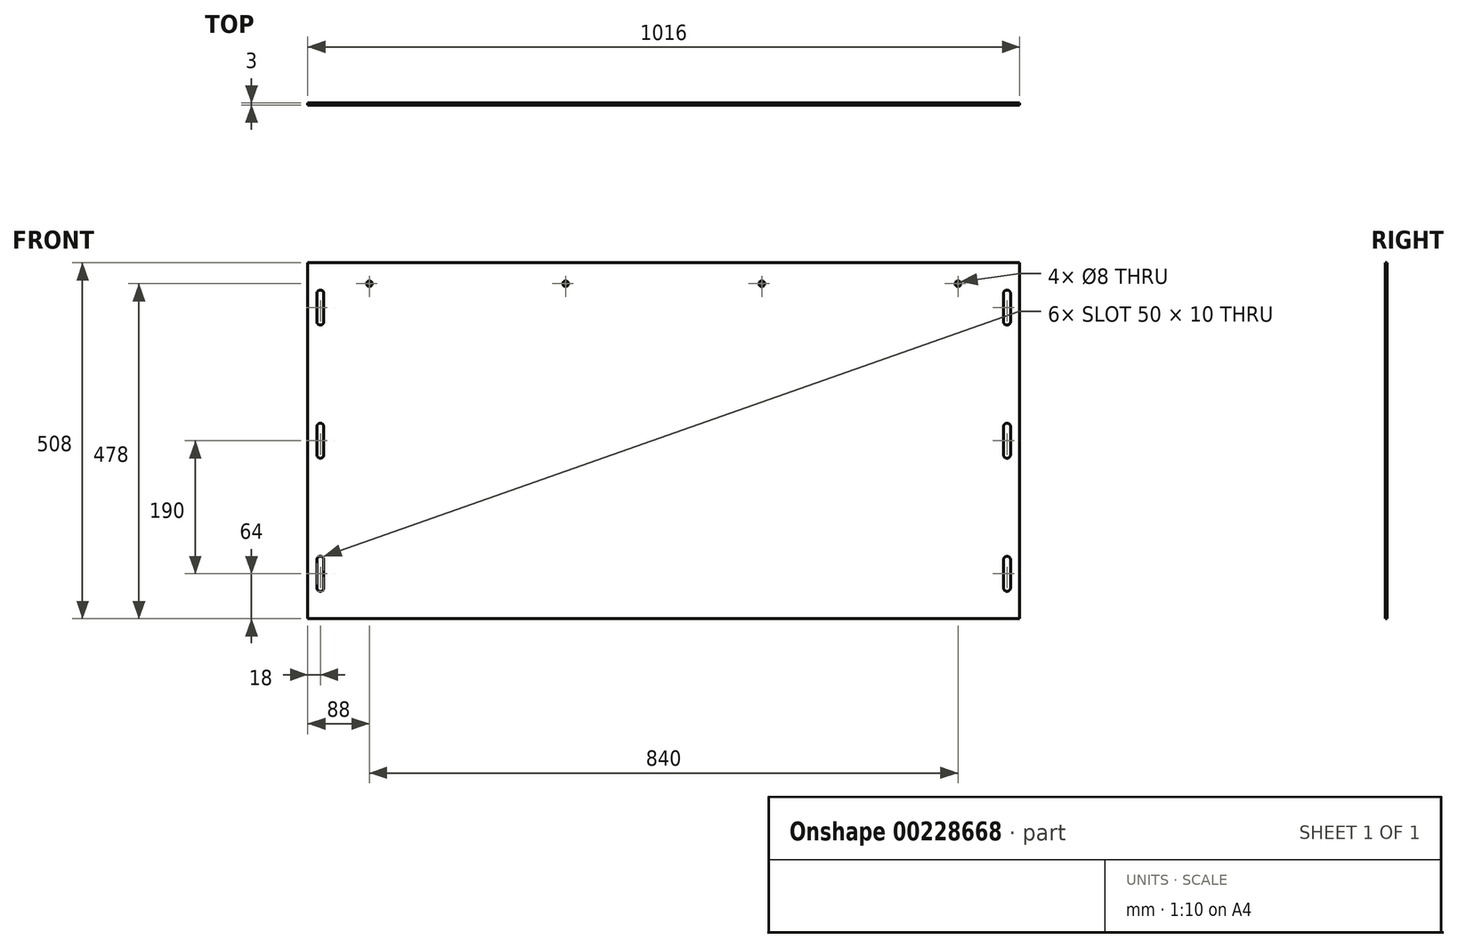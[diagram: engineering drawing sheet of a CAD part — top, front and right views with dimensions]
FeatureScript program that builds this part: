
annotation { "Feature Type Name" : "Feature", "Feature Type Description" : "" }
export const myFeature = defineFeature(function(context is Context, id is Id, definition is map)
    precondition{}
    {
        {
            var Q0;
            Q0=qCreatedBy(makeId("Front.planeOp"),FACE);
            var sketch = newSketch(context, id + "F0", { "sketchPlane" : qUnion([Q0])});
            skLineSegment(sketch, "E0.bottom", {"start": v(0, 0) * mm, "end": v(1016, 0) * mm});
            skLineSegment(sketch, "E0.top", {"start": v(0, 508) * mm, "end": v(1016, 508) * mm});
            skLineSegment(sketch, "E0.left", {"start": v(0, 0) * mm, "end": v(0, 508) * mm});
            skLineSegment(sketch, "E0.right", {"start": v(1016, 0) * mm, "end": v(1016, 508) * mm});
            skLineSegment(sketch, "E1", {"start": v(18, 508) * mm, "end": v(18, 0) * mm, "construction": true});
            skLineSegment(sketch, "E2", {"start": v(998, 508) * mm, "end": v(998, 0) * mm, "construction": true});
            skArc(sketch, "E3", {"start": v(23, 464) * mm, "mid": v(18, 469) * mm, "end": v(13, 464) * mm});
            skArc(sketch, "E4", {"start": v(13, 424) * mm, "mid": v(18, 419) * mm, "end": v(23, 424) * mm});
            skArc(sketch, "E5", {"start": v(23, 274) * mm, "mid": v(18, 279) * mm, "end": v(13, 274) * mm});
            skArc(sketch, "E6", {"start": v(13, 234) * mm, "mid": v(18, 229) * mm, "end": v(23, 234) * mm});
            skArc(sketch, "E7", {"start": v(23, 84) * mm, "mid": v(18, 89) * mm, "end": v(13, 84) * mm});
            skArc(sketch, "E8", {"start": v(13, 44) * mm, "mid": v(18, 39) * mm, "end": v(23, 44) * mm});
            skLineSegment(sketch, "E9", {"start": v(13, 464) * mm, "end": v(13, 424) * mm});
            skLineSegment(sketch, "E10", {"start": v(23, 464) * mm, "end": v(23, 424) * mm});
            skLineSegment(sketch, "E11", {"start": v(13, 274) * mm, "end": v(13, 234) * mm});
            skLineSegment(sketch, "E12", {"start": v(23, 274) * mm, "end": v(23, 234) * mm});
            skLineSegment(sketch, "E13", {"start": v(13, 84) * mm, "end": v(13, 44) * mm});
            skLineSegment(sketch, "E14", {"start": v(23, 84) * mm, "end": v(23, 44) * mm});
            skArc(sketch, "E15", {"start": v(1003, 464) * mm, "mid": v(998, 469) * mm, "end": v(993, 464) * mm});
            skArc(sketch, "E16", {"start": v(993, 424) * mm, "mid": v(998, 419) * mm, "end": v(1003, 424) * mm});
            skArc(sketch, "E17", {"start": v(1003, 274) * mm, "mid": v(998, 279) * mm, "end": v(993, 274) * mm});
            skArc(sketch, "E18", {"start": v(993, 234) * mm, "mid": v(998, 229) * mm, "end": v(1003, 234) * mm});
            skArc(sketch, "E19", {"start": v(993, 44) * mm, "mid": v(998, 39) * mm, "end": v(1003, 44) * mm});
            skArc(sketch, "E20", {"start": v(1003, 84) * mm, "mid": v(998, 89) * mm, "end": v(993, 84) * mm});
            skLineSegment(sketch, "E21", {"start": v(993, 464) * mm, "end": v(993, 424) * mm});
            skLineSegment(sketch, "E22", {"start": v(1003, 464) * mm, "end": v(1003, 424) * mm});
            skLineSegment(sketch, "E23", {"start": v(993, 274) * mm, "end": v(993, 234) * mm});
            skLineSegment(sketch, "E24", {"start": v(1003, 274) * mm, "end": v(1003, 234) * mm});
            skLineSegment(sketch, "E25", {"start": v(993, 84) * mm, "end": v(993, 44) * mm});
            skLineSegment(sketch, "E26", {"start": v(1003, 84) * mm, "end": v(1003, 44) * mm});
            skLineSegment(sketch, "E27", {"start": v(88, 478) * mm, "end": v(928, 478) * mm, "construction": true});
            skLineSegment(sketch, "E28", {"start": v(508, 508) * mm, "end": v(508, 478) * mm, "construction": true});
            skCircle(sketch, "E29", {"center": v(88, 478) * mm, "radius": 4 * mm});
            skCircle(sketch, "E30", {"center": v(368, 478) * mm, "radius": 4 * mm});
            skCircle(sketch, "E31", {"center": v(648, 478) * mm, "radius": 4 * mm});
            skCircle(sketch, "E32", {"center": v(928, 478) * mm, "radius": 4 * mm});
            skSolve(sketch);
        }
        {
            var Q0;
            Q0 = qSketchRegion(id + "F0", true);
            extrude(context, id + "F1", {"entities" : qUnion([Q0]), "depth" : 3 * mm});
        }
    });
